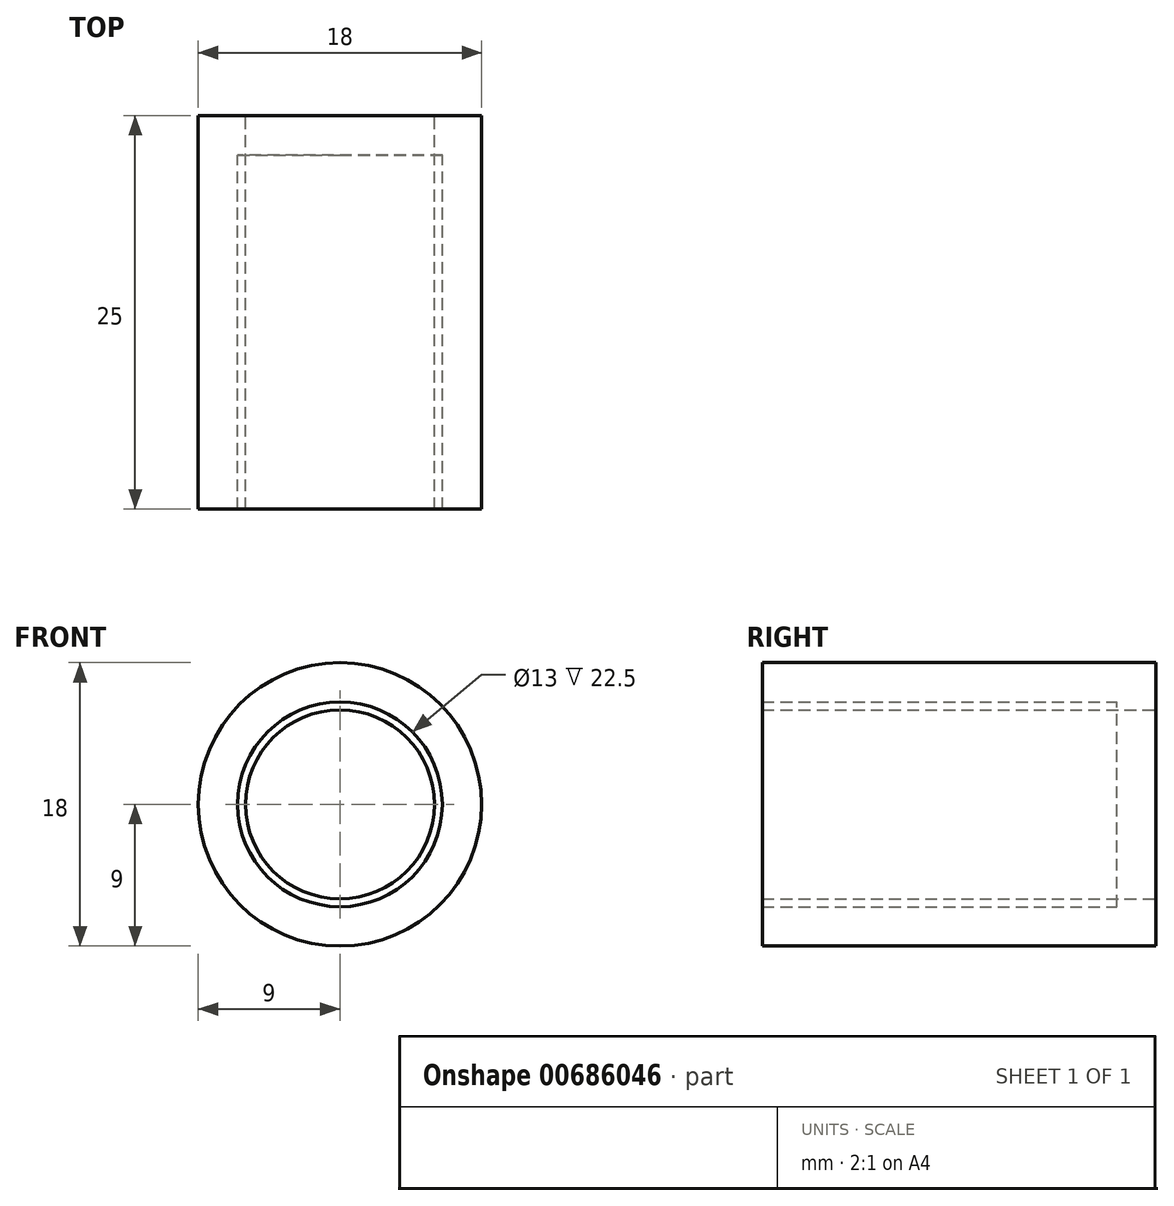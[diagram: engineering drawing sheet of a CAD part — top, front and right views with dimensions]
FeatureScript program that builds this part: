
annotation { "Feature Type Name" : "Feature", "Feature Type Description" : "" }
export const myFeature = defineFeature(function(context is Context, id is Id, definition is map)
    precondition{}
    {
        {
            var Q0;
            Q0=qCreatedBy(makeId("Front.planeOp"),FACE);
            var sketch = newSketch(context, id + "F0", { "sketchPlane" : qUnion([Q0])});
            skCircle(sketch, "E0", {"center": v(0, 0) * mm, "radius": 9 * mm});
            skSolve(sketch);
        }
        {
            var Q0;
            Q0=makeQuery(id+"F0.imprint","IMPRINT",FACE,{"disambiguationData":[TD([[makeQuery(id+"F0.imprint","IMPRINT",EDGE,{"derivedFrom":sQuery(id+"F0.wireOp",EDGE,"E0")}),1.0]])]});
            var sketch = newSketch(context, id + "F1", { "sketchPlane" : qUnion([Q0])});
            skCircle(sketch, "E1", {"center": v(0, 0) * mm, "radius": 6 * mm});
            skSolve(sketch);
        }
        {
            var Q0;
            Q0=makeQuery(id+"F0.imprint","IMPRINT",FACE,{"disambiguationData":[TD([[makeQuery(id+"F0.imprint","IMPRINT",EDGE,{"derivedFrom":sQuery(id+"F0.wireOp",EDGE,"E0")}),1.0]])]});
            var Q1;
            Q1=makeQuery(id+"F1.imprint","IMPRINT",FACE,{"disambiguationData":[TD([[makeQuery(id+"F1.imprint","IMPRINT",EDGE,{"derivedFrom":sQuery(id+"F1.wireOp",EDGE,"E1")}),1.0]])]});
            extrude(context, id + "F2", {"entities" : qUnion([Q0, Q1]), "depth" : 25 * mm, "offsetDistance" : 25 * mm});
        }
        {
            var Q0;
            Q0=makeQuery(id+"F2.opExtrude","CAP_FACE",FACE,{"disambiguationData":[OSD([sQuery(id+"F0.wireOp",EDGE,"E0")])],"isStart":false});
            shell(context, id + "F3", {"entities" : qUnion([Q0]), "thickness" : 2.5 * mm});
        }
    });
